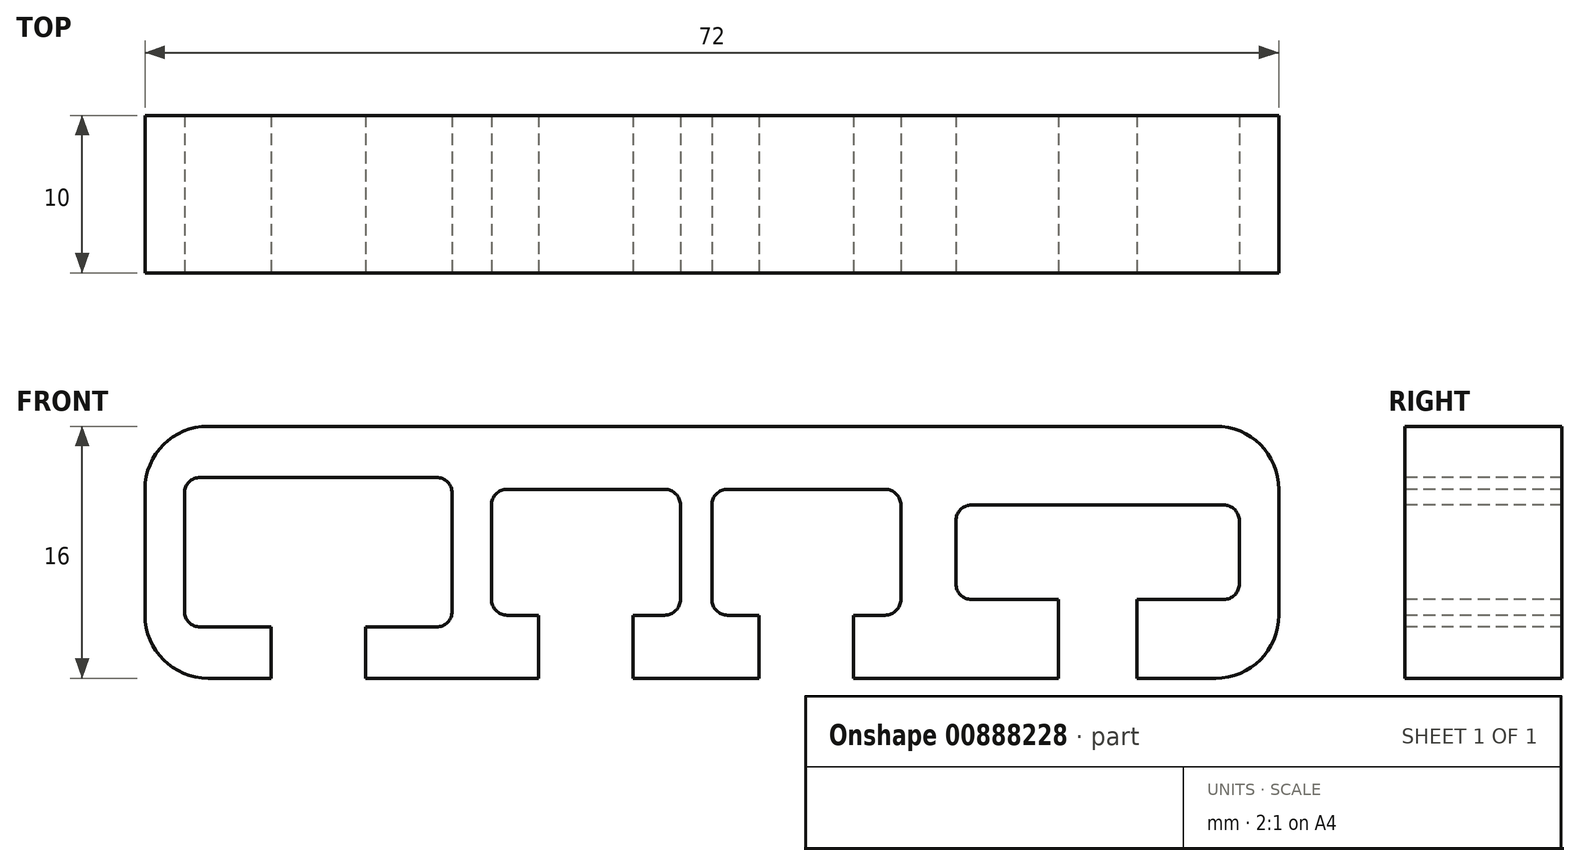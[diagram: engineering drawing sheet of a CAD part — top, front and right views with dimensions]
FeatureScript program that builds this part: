
annotation { "Feature Type Name" : "Feature", "Feature Type Description" : "" }
export const myFeature = defineFeature(function(context is Context, id is Id, definition is map)
    precondition{}
    {
        {
            var Q0;
            Q0=qCreatedBy(makeId("Top.planeOp"),FACE);
            var sketch = newSketch(context, id + "F0", { "sketchPlane" : qUnion([Q0])});
            skLineSegment(sketch, "E0.bottom", {"start": v(-36, 20) * mm, "end": v(36, 20) * mm});
            skLineSegment(sketch, "E0.top", {"start": v(-36, -20) * mm, "end": v(36, -20) * mm});
            skLineSegment(sketch, "E0.left", {"start": v(-36, 20) * mm, "end": v(-36, -20) * mm});
            skLineSegment(sketch, "E0.right", {"start": v(36, 20) * mm, "end": v(36, -20) * mm});
            skPoint(sketch, "E0.middle", {"position": v(0, 0) * mm});
            skSolve(sketch);
        }
        {
            var Q0;
            Q0=makeQuery(id+"F0.imprint","IMPRINT",FACE,{"disambiguationData":[TD([[makeQuery(id+"F0.imprint","IMPRINT",EDGE,{"derivedFrom":sQuery(id+"F0.wireOp",EDGE,"E0.bottom")}),-1.0]])]});
            extrude(context, id + "F1", {"entities" : qUnion([Q0]), "depth" : 16 * mm, "offsetDistance" : 25 * mm});
        }
        {
            var Q0;
            Q0=makeQuery(id+"F1.opExtrude","SWEPT_FACE",FACE,{"disambiguationData":[OSD([sQuery(id+"F0.wireOp",EDGE,"E0.top")])]});
            var sketch = newSketch(context, id + "F2", { "sketchPlane" : qUnion([Q0])});
            skLineSegment(sketch, "E1", {"start": v(0, 0) * mm, "end": v(0, 16) * mm, "construction": true});
            skLineSegment(sketch, "E2.bottom", {"start": v(-36, 0) * mm, "end": v(36, 0) * mm, "construction": true});
            skLineSegment(sketch, "E2.top", {"start": v(-36, 16) * mm, "end": v(36, 16) * mm, "construction": true});
            skLineSegment(sketch, "E2.left", {"start": v(-36, 0) * mm, "end": v(-36, 16) * mm, "construction": true});
            skLineSegment(sketch, "E2.right", {"start": v(36, 0) * mm, "end": v(36, 16) * mm, "construction": true});
            skLineSegment(sketch, "E3", {"start": v(-36, 8) * mm, "end": v(36, 8) * mm, "construction": true});
            skPoint(sketch, "E4.middle", {"position": v(0, 8) * mm});
            skLineSegment(sketch, "E5.bottom", {"start": v(-14, 12) * mm, "end": v(-2, 12) * mm});
            skLineSegment(sketch, "E5.top", {"start": v(-14, 4) * mm, "end": v(-2, 4) * mm});
            skLineSegment(sketch, "E5.left", {"start": v(-14, 12) * mm, "end": v(-14, 4) * mm});
            skLineSegment(sketch, "E5.right", {"start": v(-2, 12) * mm, "end": v(-2, 4) * mm});
            skPoint(sketch, "E5.middle", {"position": v(-8, 8) * mm});
            skLineSegment(sketch, "E6.bottom", {"start": v(0, 12) * mm, "end": v(12, 12) * mm});
            skLineSegment(sketch, "E6.top", {"start": v(0, 4) * mm, "end": v(12, 4) * mm});
            skLineSegment(sketch, "E6.left", {"start": v(0, 12) * mm, "end": v(0, 4) * mm});
            skLineSegment(sketch, "E6.right", {"start": v(12, 12) * mm, "end": v(12, 4) * mm});
            skPoint(sketch, "E6.middle", {"position": v(6, 8) * mm});
            skLineSegment(sketch, "E7.bottom", {"start": v(15.5, 11) * mm, "end": v(33.5, 11) * mm});
            skLineSegment(sketch, "E7.top", {"start": v(15.5, 5) * mm, "end": v(33.5, 5) * mm});
            skLineSegment(sketch, "E7.left", {"start": v(15.5, 11) * mm, "end": v(15.5, 5) * mm});
            skLineSegment(sketch, "E7.right", {"start": v(33.5, 11) * mm, "end": v(33.5, 5) * mm});
            skPoint(sketch, "E7.middle", {"position": v(24.5, 8) * mm});
            skLineSegment(sketch, "E8.bottom", {"start": v(-33.5, 12.75) * mm, "end": v(-16.5, 12.75) * mm});
            skLineSegment(sketch, "E8.top", {"start": v(-33.5, 3.25) * mm, "end": v(-16.5, 3.25) * mm});
            skLineSegment(sketch, "E8.left", {"start": v(-33.5, 12.75) * mm, "end": v(-33.5, 3.25) * mm});
            skLineSegment(sketch, "E8.right", {"start": v(-16.5, 12.75) * mm, "end": v(-16.5, 3.25) * mm});
            skPoint(sketch, "E8.middle", {"position": v(-25, 8) * mm});
            skSolve(sketch);
        }
        {
            var Q0;
            Q0=makeQuery(id+"F2.imprint","IMPRINT",FACE,{"disambiguationData":[TD([[makeQuery(id+"F2.imprint","IMPRINT",EDGE,{"derivedFrom":sQuery(id+"F2.wireOp",EDGE,"E5.bottom")}),1.0]])]});
            var sketch = newSketch(context, id + "F3", { "sketchPlane" : qUnion([Q0])});
            skLineSegment(sketch, "E9.0", {"start": v(-33.5, 12.75) * mm, "end": v(-16.5, 12.75) * mm});
            skLineSegment(sketch, "E9.1", {"start": v(-16.5, 12.75) * mm, "end": v(-16.5, 3.25) * mm});
            skLineSegment(sketch, "E9.2", {"start": v(-33.5, 12.75) * mm, "end": v(-33.5, 3.25) * mm});
            skLineSegment(sketch, "E9.3", {"start": v(-33.5, 3.25) * mm, "end": v(-16.5, 3.25) * mm});
            skSolve(sketch);
        }
        {
            var Q0;
            Q0=makeQuery(id+"F2.imprint","IMPRINT",FACE,{"disambiguationData":[TD([[makeQuery(id+"F2.imprint","IMPRINT",EDGE,{"derivedFrom":sQuery(id+"F2.wireOp",EDGE,"E5.bottom")}),1.0]])]});
            var sketch = newSketch(context, id + "F4", { "sketchPlane" : qUnion([Q0])});
            skLineSegment(sketch, "E10.0", {"start": v(-14, 12) * mm, "end": v(-2, 12) * mm});
            skLineSegment(sketch, "E10.1", {"start": v(-14, 12) * mm, "end": v(-14, 4) * mm});
            skLineSegment(sketch, "E10.2", {"start": v(-14, 4) * mm, "end": v(-2, 4) * mm});
            skLineSegment(sketch, "E10.3", {"start": v(-2, 12) * mm, "end": v(-2, 4) * mm});
            skPoint(sketch, "E10.4", {"position": v(-8, 12) * mm});
            skSolve(sketch);
        }
        {
            var Q0;
            Q0=makeQuery(id+"F2.imprint","IMPRINT",FACE,{"disambiguationData":[TD([[makeQuery(id+"F2.imprint","IMPRINT",EDGE,{"derivedFrom":sQuery(id+"F2.wireOp",EDGE,"E5.bottom")}),1.0]])]});
            var sketch = newSketch(context, id + "F5", { "sketchPlane" : qUnion([Q0])});
            skLineSegment(sketch, "E11.0", {"start": v(0, 12) * mm, "end": v(12, 12) * mm});
            skLineSegment(sketch, "E11.1", {"start": v(12, 12) * mm, "end": v(12, 4) * mm});
            skLineSegment(sketch, "E11.2", {"start": v(0, 4) * mm, "end": v(12, 4) * mm});
            skLineSegment(sketch, "E11.3", {"start": v(0, 12) * mm, "end": v(0, 4) * mm});
            skSolve(sketch);
        }
        {
            var Q0;
            Q0=makeQuery(id+"F2.imprint","IMPRINT",FACE,{"disambiguationData":[TD([[makeQuery(id+"F2.imprint","IMPRINT",EDGE,{"derivedFrom":sQuery(id+"F2.wireOp",EDGE,"E5.bottom")}),1.0]])]});
            var sketch = newSketch(context, id + "F6", { "sketchPlane" : qUnion([Q0])});
            skLineSegment(sketch, "E12.0", {"start": v(15.5, 11) * mm, "end": v(33.5, 11) * mm});
            skLineSegment(sketch, "E12.1", {"start": v(15.5, 11) * mm, "end": v(15.5, 5) * mm});
            skLineSegment(sketch, "E12.2", {"start": v(15.5, 5) * mm, "end": v(33.5, 5) * mm});
            skLineSegment(sketch, "E12.3", {"start": v(33.5, 11) * mm, "end": v(33.5, 5) * mm});
            skSolve(sketch);
        }
        {
            var Q0;
            Q0 = qSketchRegion(id + "F3", true);
            extrude(context, id + "F7", {"entities" : qUnion([Q0]), "operationType" : NewBodyOperationType.REMOVE, "oppositeDirection" : true, "depth" : 35 * mm, "offsetDistance" : 25 * mm});
        }
        {
            var Q0;
            Q0 = qSketchRegion(id + "F4", true);
            extrude(context, id + "F8", {"entities" : qUnion([Q0]), "operationType" : NewBodyOperationType.REMOVE, "oppositeDirection" : true, "depth" : 20 * mm, "offsetDistance" : 25 * mm});
        }
        {
            var Q0;
            Q0 = qSketchRegion(id + "F5", true);
            extrude(context, id + "F9", {"entities" : qUnion([Q0]), "operationType" : NewBodyOperationType.REMOVE, "oppositeDirection" : true, "depth" : 28 * mm, "offsetDistance" : 25 * mm});
        }
        {
            var Q0;
            Q0 = qSketchRegion(id + "F6", true);
            extrude(context, id + "F10", {"entities" : qUnion([Q0]), "operationType" : NewBodyOperationType.REMOVE, "oppositeDirection" : true, "depth" : 11 * mm, "offsetDistance" : 25 * mm});
        }
        {
            var Q0;
            Q0=makeQuery(id+"F2.imprint","IMPRINT",FACE,{"disambiguationData":[TD([[makeQuery(id+"F2.imprint","IMPRINT",EDGE,{"derivedFrom":sQuery(id+"F2.wireOp",EDGE,"E8.bottom")}),-1.0]])]});
            var sketch = newSketch(context, id + "F11", { "sketchPlane" : qUnion([Q0])});
            skLineSegment(sketch, "E13.0", {"start": v(-33.5, 12.75) * mm, "end": v(-16.5, 12.75) * mm, "construction": true});
            skLineSegment(sketch, "E13.1", {"start": v(-33.5, 3.25) * mm, "end": v(-16.5, 3.25) * mm, "construction": true});
            skLineSegment(sketch, "E13.2", {"start": v(-14, 12) * mm, "end": v(-2, 12) * mm, "construction": true});
            skLineSegment(sketch, "E13.3", {"start": v(-14, 4) * mm, "end": v(-2, 4) * mm, "construction": true});
            skLineSegment(sketch, "E13.4", {"start": v(0, 12) * mm, "end": v(12, 12) * mm, "construction": true});
            skLineSegment(sketch, "E13.5", {"start": v(0, 4) * mm, "end": v(12, 4) * mm, "construction": true});
            skLineSegment(sketch, "E13.6", {"start": v(15.5, 11) * mm, "end": v(33.5, 11) * mm, "construction": true});
            skLineSegment(sketch, "E13.7", {"start": v(15.5, 5) * mm, "end": v(33.5, 5) * mm, "construction": true});
            skLineSegment(sketch, "E14", {"start": v(-25, 12.75) * mm, "end": v(-25, 3.25) * mm, "construction": true});
            skLineSegment(sketch, "E15", {"start": v(-8, 12) * mm, "end": v(-8, 4) * mm, "construction": true});
            skLineSegment(sketch, "E16", {"start": v(6, 12) * mm, "end": v(6, 4) * mm, "construction": true});
            skLineSegment(sketch, "E17", {"start": v(24.5, 11) * mm, "end": v(24.5, 5) * mm, "construction": true});
            skCircle(sketch, "E18", {"center": v(-25, 8) * mm, "radius": 3.25 * mm});
            skCircle(sketch, "E19", {"center": v(-8, 8) * mm, "radius": 3.25 * mm});
            skCircle(sketch, "E20", {"center": v(6, 8) * mm, "radius": 3.25 * mm});
            skCircle(sketch, "E21", {"center": v(24.5, 8) * mm, "radius": 3 * mm});
            skSolve(sketch);
        }
        {
            var Q0;
            Q0 = qSketchRegion(id + "F11", true);
            extrude(context, id + "F12", {"entities" : qUnion([Q0]), "operationType" : NewBodyOperationType.REMOVE, "endBound" : BoundingType.THROUGH_ALL, "oppositeDirection" : true, "depth" : 25 * mm, "offsetDistance" : 25 * mm});
        }
        {
            var Q0;
            Q0=makeQuery(id+"F1.opExtrude","CAP_FACE",FACE,{"disambiguationData":[OSD([sQuery(id+"F0.wireOp",EDGE,"E0.bottom"),sQuery(id+"F0.wireOp",EDGE,"E0.top"),sQuery(id+"F0.wireOp",EDGE,"E0.left"),sQuery(id+"F0.wireOp",EDGE,"E0.right")])],"isStart":true});
            var sketch = newSketch(context, id + "F13", { "sketchPlane" : qUnion([Q0])});
            skLineSegment(sketch, "E22.0", {"start": v(-33.5, 20) * mm, "end": v(-16.5, 20) * mm});
            skLineSegment(sketch, "E22.1", {"start": v(-14, 20) * mm, "end": v(-2, 20) * mm});
            skLineSegment(sketch, "E22.2", {"start": v(0, 20) * mm, "end": v(12, 20) * mm});
            skLineSegment(sketch, "E22.3", {"start": v(15.5, 20) * mm, "end": v(33.5, 20) * mm});
            skLineSegment(sketch, "E23", {"start": v(-25, 20) * mm, "end": v(-25, -20) * mm, "construction": true});
            skLineSegment(sketch, "E24", {"start": v(-8, 20) * mm, "end": v(-8, -20) * mm, "construction": true});
            skLineSegment(sketch, "E25", {"start": v(6, 20) * mm, "end": v(6, -20) * mm, "construction": true});
            skLineSegment(sketch, "E26", {"start": v(24.5, 20) * mm, "end": v(24.5, -20) * mm, "construction": true});
            skLineSegment(sketch, "E27.bottom", {"start": v(-28, -20) * mm, "end": v(-22, -20) * mm});
            skLineSegment(sketch, "E27.top", {"start": v(-28, 20) * mm, "end": v(-22, 20) * mm});
            skLineSegment(sketch, "E27.left", {"start": v(-28, -20) * mm, "end": v(-28, 20) * mm});
            skLineSegment(sketch, "E27.right", {"start": v(-22, -20) * mm, "end": v(-22, 20) * mm});
            skPoint(sketch, "E27.middle", {"position": v(-25, 0) * mm});
            skLineSegment(sketch, "E28.bottom", {"start": v(-11, -20) * mm, "end": v(-5, -20) * mm});
            skLineSegment(sketch, "E28.top", {"start": v(-11, 20) * mm, "end": v(-5, 20) * mm});
            skLineSegment(sketch, "E28.left", {"start": v(-11, -20) * mm, "end": v(-11, 20) * mm});
            skLineSegment(sketch, "E28.right", {"start": v(-5, -20) * mm, "end": v(-5, 20) * mm});
            skPoint(sketch, "E28.middle", {"position": v(-8, 0) * mm});
            skLineSegment(sketch, "E29.bottom", {"start": v(3, -20) * mm, "end": v(9, -20) * mm});
            skLineSegment(sketch, "E29.top", {"start": v(3, 20) * mm, "end": v(9, 20) * mm});
            skLineSegment(sketch, "E29.left", {"start": v(3, -20) * mm, "end": v(3, 20) * mm});
            skLineSegment(sketch, "E29.right", {"start": v(9, -20) * mm, "end": v(9, 20) * mm});
            skPoint(sketch, "E29.middle", {"position": v(6, 0) * mm});
            skLineSegment(sketch, "E30.bottom", {"start": v(22, -20) * mm, "end": v(27, -20) * mm});
            skLineSegment(sketch, "E30.top", {"start": v(22, 20) * mm, "end": v(27, 20) * mm});
            skLineSegment(sketch, "E30.left", {"start": v(22, -20) * mm, "end": v(22, 20) * mm});
            skLineSegment(sketch, "E30.right", {"start": v(27, -20) * mm, "end": v(27, 20) * mm});
            skPoint(sketch, "E30.middle", {"position": v(24.5, 0) * mm});
            skSolve(sketch);
        }
        {
            var Q0;
            Q0 = qSketchRegion(id + "F13", true);
            extrude(context, id + "F14", {"entities" : qUnion([Q0]), "operationType" : NewBodyOperationType.REMOVE, "oppositeDirection" : true, "depth" : 8 * mm, "offsetDistance" : 25 * mm});
        }
        {
            var Q0;
            Q0=makeQuery(id+"F10.boolean.opBoolean","COPY",EDGE,{"derivedFrom":makeQuery(id+"F10.opExtrude","SWEPT_EDGE",EDGE,{"disambiguationData":[OSD([sQuery(id+"F6.wireOp",EDGE,"E12.2"),sQuery(id+"F6.wireOp",EDGE,"E12.3")])]})});
            var Q1;
            Q1=makeQuery(id+"F10.boolean.opBoolean","COPY",EDGE,{"derivedFrom":makeQuery(id+"F10.opExtrude","SWEPT_EDGE",EDGE,{"disambiguationData":[OSD([sQuery(id+"F6.wireOp",EDGE,"E12.0"),sQuery(id+"F6.wireOp",EDGE,"E12.3")])]})});
            var Q2;
            Q2=makeQuery(id+"F9.boolean.opBoolean","COPY",EDGE,{"derivedFrom":makeQuery(id+"F9.opExtrude","SWEPT_EDGE",EDGE,{"disambiguationData":[OSD([sQuery(id+"F5.wireOp",EDGE,"E11.0"),sQuery(id+"F5.wireOp",EDGE,"E11.1")])]})});
            var Q3;
            Q3=makeQuery(id+"F8.boolean.opBoolean","COPY",EDGE,{"derivedFrom":makeQuery(id+"F8.opExtrude","SWEPT_EDGE",EDGE,{"disambiguationData":[OSD([sQuery(id+"F4.wireOp",EDGE,"E10.0"),sQuery(id+"F4.wireOp",EDGE,"E10.3")])]})});
            var Q4;
            Q4=makeQuery(id+"F7.boolean.opBoolean","COPY",EDGE,{"derivedFrom":makeQuery(id+"F7.opExtrude","SWEPT_EDGE",EDGE,{"disambiguationData":[OSD([sQuery(id+"F3.wireOp",EDGE,"E9.0"),sQuery(id+"F3.wireOp",EDGE,"E9.1")])]})});
            var Q5;
            Q5=makeQuery(id+"F7.boolean.opBoolean","COPY",EDGE,{"derivedFrom":makeQuery(id+"F7.opExtrude","SWEPT_EDGE",EDGE,{"disambiguationData":[OSD([sQuery(id+"F3.wireOp",EDGE,"E9.2"),sQuery(id+"F3.wireOp",EDGE,"E9.3")])]})});
            var Q6;
            Q6=makeQuery(id+"F8.boolean.opBoolean","COPY",EDGE,{"derivedFrom":makeQuery(id+"F8.opExtrude","SWEPT_EDGE",EDGE,{"disambiguationData":[OSD([sQuery(id+"F4.wireOp",EDGE,"E10.1"),sQuery(id+"F4.wireOp",EDGE,"E10.2")])]})});
            var Q7;
            Q7=makeQuery(id+"F9.boolean.opBoolean","COPY",EDGE,{"derivedFrom":makeQuery(id+"F9.opExtrude","SWEPT_EDGE",EDGE,{"disambiguationData":[OSD([sQuery(id+"F5.wireOp",EDGE,"E11.2"),sQuery(id+"F5.wireOp",EDGE,"E11.3")])]})});
            var Q8;
            Q8=makeQuery(id+"F10.boolean.opBoolean","COPY",EDGE,{"derivedFrom":makeQuery(id+"F10.opExtrude","SWEPT_EDGE",EDGE,{"disambiguationData":[OSD([sQuery(id+"F6.wireOp",EDGE,"E12.1"),sQuery(id+"F6.wireOp",EDGE,"E12.2")])]})});
            var Q9;
            Q9=makeQuery(id+"F10.boolean.opBoolean","COPY",EDGE,{"derivedFrom":makeQuery(id+"F10.opExtrude","SWEPT_EDGE",EDGE,{"disambiguationData":[OSD([sQuery(id+"F6.wireOp",EDGE,"E12.0"),sQuery(id+"F6.wireOp",EDGE,"E12.1")])]})});
            var Q10;
            Q10=makeQuery(id+"F9.boolean.opBoolean","COPY",EDGE,{"derivedFrom":makeQuery(id+"F9.opExtrude","SWEPT_EDGE",EDGE,{"disambiguationData":[OSD([sQuery(id+"F5.wireOp",EDGE,"E11.0"),sQuery(id+"F5.wireOp",EDGE,"E11.3")])]})});
            var Q11;
            Q11=makeQuery(id+"F8.boolean.opBoolean","COPY",EDGE,{"derivedFrom":makeQuery(id+"F8.opExtrude","SWEPT_EDGE",EDGE,{"disambiguationData":[OSD([sQuery(id+"F4.wireOp",EDGE,"E10.0"),sQuery(id+"F4.wireOp",EDGE,"E10.1")])]})});
            var Q12;
            Q12=makeQuery(id+"F7.boolean.opBoolean","COPY",EDGE,{"derivedFrom":makeQuery(id+"F7.opExtrude","SWEPT_EDGE",EDGE,{"disambiguationData":[OSD([sQuery(id+"F3.wireOp",EDGE,"E9.0"),sQuery(id+"F3.wireOp",EDGE,"E9.2")])]})});
            var Q13;
            Q13=makeQuery(id+"F9.boolean.opBoolean","COPY",EDGE,{"derivedFrom":makeQuery(id+"F9.opExtrude","SWEPT_EDGE",EDGE,{"disambiguationData":[OSD([sQuery(id+"F5.wireOp",EDGE,"E11.1"),sQuery(id+"F5.wireOp",EDGE,"E11.2")])]})});
            var Q14;
            Q14=makeQuery(id+"F8.boolean.opBoolean","COPY",EDGE,{"derivedFrom":makeQuery(id+"F8.opExtrude","SWEPT_EDGE",EDGE,{"disambiguationData":[OSD([sQuery(id+"F4.wireOp",EDGE,"E10.2"),sQuery(id+"F4.wireOp",EDGE,"E10.3")])]})});
            var Q15;
            Q15=makeQuery(id+"F7.boolean.opBoolean","COPY",EDGE,{"derivedFrom":makeQuery(id+"F7.opExtrude","SWEPT_EDGE",EDGE,{"disambiguationData":[OSD([sQuery(id+"F3.wireOp",EDGE,"E9.1"),sQuery(id+"F3.wireOp",EDGE,"E9.3")])]})});
            var Q16;
            Q16=makeQuery(id+"F14.boolean.opBoolean","COPY",EDGE,{"derivedFrom":makeQuery(id+"F14.opExtrude","CAP_EDGE",EDGE,{"disambiguationData":[OSD([sQuery(id+"F13.wireOp",EDGE,"E30.left")])],"isStart":true})});
            var Q17;
            Q17=makeQuery(id+"F14.boolean.opBoolean","COPY",EDGE,{"derivedFrom":makeQuery(id+"F14.opExtrude","CAP_EDGE",EDGE,{"disambiguationData":[OSD([sQuery(id+"F13.wireOp",EDGE,"E30.right")])],"isStart":true})});
            var Q18;
            Q18=makeQuery(id+"F14.boolean.opBoolean","COPY",EDGE,{"derivedFrom":makeQuery(id+"F14.opExtrude","CAP_EDGE",EDGE,{"disambiguationData":[OSD([sQuery(id+"F13.wireOp",EDGE,"E29.left")])],"isStart":true})});
            var Q19;
            Q19=makeQuery(id+"F14.boolean.opBoolean","COPY",EDGE,{"derivedFrom":makeQuery(id+"F14.opExtrude","CAP_EDGE",EDGE,{"disambiguationData":[OSD([sQuery(id+"F13.wireOp",EDGE,"E29.right")])],"isStart":true})});
            var Q20;
            Q20=makeQuery(id+"F14.boolean.opBoolean","COPY",EDGE,{"derivedFrom":makeQuery(id+"F14.opExtrude","CAP_EDGE",EDGE,{"disambiguationData":[OSD([sQuery(id+"F13.wireOp",EDGE,"E28.left")])],"isStart":true})});
            var Q21;
            Q21=makeQuery(id+"F14.boolean.opBoolean","COPY",EDGE,{"derivedFrom":makeQuery(id+"F14.opExtrude","CAP_EDGE",EDGE,{"disambiguationData":[OSD([sQuery(id+"F13.wireOp",EDGE,"E28.right")])],"isStart":true})});
            var Q22;
            Q22=makeQuery(id+"F14.boolean.opBoolean","COPY",EDGE,{"derivedFrom":makeQuery(id+"F14.opExtrude","CAP_EDGE",EDGE,{"disambiguationData":[OSD([sQuery(id+"F13.wireOp",EDGE,"E27.left")])],"isStart":true})});
            var Q23;
            Q23=makeQuery(id+"F14.boolean.opBoolean","COPY",EDGE,{"derivedFrom":makeQuery(id+"F14.opExtrude","CAP_EDGE",EDGE,{"disambiguationData":[OSD([sQuery(id+"F13.wireOp",EDGE,"E27.right")])],"isStart":true})});
            fillet(context, id + "F15", {"entities" : qUnion([Q0, Q1, Q2, Q3, Q4, Q5, Q6, Q7, Q8, Q9, Q10, Q11, Q12, Q13, Q14, Q15, Q16, Q17, Q18, Q19, Q20, Q21, Q22, Q23]), "radius" : 1 * mm, "tangentPropagation" : true, "allowEdgeOverflow" : false});
        }
        {
            var Q0;
            Q0=makeQuery(id+"F1.opExtrude","CAP_EDGE",EDGE,{"disambiguationData":[OSD([sQuery(id+"F0.wireOp",EDGE,"E0.right")])],"isStart":true});
            var Q1;
            Q1=makeQuery(id+"F1.opExtrude","CAP_EDGE",EDGE,{"disambiguationData":[OSD([sQuery(id+"F0.wireOp",EDGE,"E0.right")])],"isStart":false});
            var Q2;
            Q2=makeQuery(id+"F1.opExtrude","CAP_EDGE",EDGE,{"disambiguationData":[OSD([sQuery(id+"F0.wireOp",EDGE,"E0.left")])],"isStart":true});
            var Q3;
            Q3=makeQuery(id+"F1.opExtrude","CAP_EDGE",EDGE,{"disambiguationData":[OSD([sQuery(id+"F0.wireOp",EDGE,"E0.left")])],"isStart":false});
            fillet(context, id + "F16", {"entities" : qUnion([Q0, Q1, Q2, Q3]), "radius" : 4 * mm, "tangentPropagation" : true, "allowEdgeOverflow" : false});
        }
        {
            var Q0;
            Q0=qCreatedBy(makeId("Top.planeOp"),FACE);
            var sketch = newSketch(context, id + "F17", { "sketchPlane" : qUnion([Q0])});
            skLineSegment(sketch, "E31.0", {"start": v(-36, -20) * mm, "end": v(-36, 20) * mm});
            skLineSegment(sketch, "E31.1", {"start": v(36, 20) * mm, "end": v(36, -20) * mm});
            skLineSegment(sketch, "E32", {"start": v(-36, -20) * mm, "end": v(36, -20) * mm});
            skLineSegment(sketch, "E33", {"start": v(-36, -10) * mm, "end": v(36, -10) * mm});
            skSolve(sketch);
        }
        {
            var Q0;
            Q0 = qSketchRegion(id + "F17", true);
            extrude(context, id + "F18", {"entities" : qUnion([Q0]), "operationType" : NewBodyOperationType.INTERSECT, "endBound" : BoundingType.THROUGH_ALL, "depth" : 25 * mm, "offsetDistance" : 25 * mm});
        }
    });
